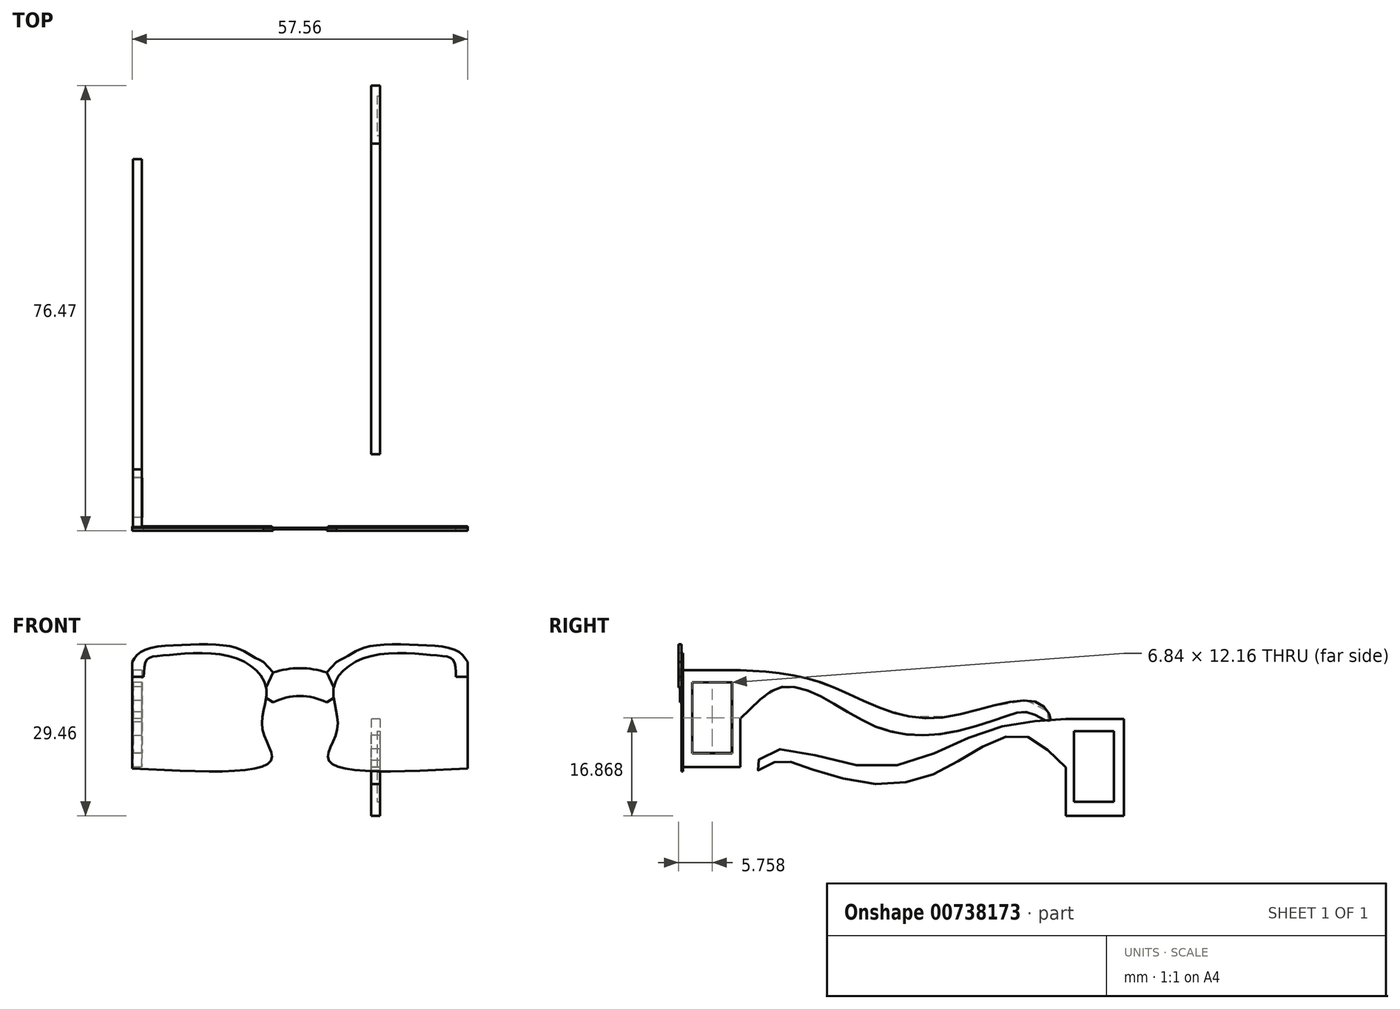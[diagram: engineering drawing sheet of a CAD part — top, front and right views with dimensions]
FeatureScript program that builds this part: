
annotation { "Feature Type Name" : "Feature", "Feature Type Description" : "" }
export const myFeature = defineFeature(function(context is Context, id is Id, definition is map)
    precondition{}
    {
        {
            var Q0;
            Q0=qCreatedBy(makeId("Front.planeOp"),FACE);
            var sketch = newSketch(context, id + "F0", { "sketchPlane" : qUnion([Q0])});
            skLineSegment(sketch, "E0", {"start": v(-26.3, 9.76) * mm, "end": v(-26.3, -8.53) * mm});
            skFitSpline(sketch, "E1", {"points": [v(-26.3, 9.76) * mm, v(-24.5, 11.69) * mm, v(-17.15, 12.72) * mm, v(-8.91, 12.33) * mm, v(-6.2, 11.04) * mm, v(-3.76, 9.76) * mm], "startDerivative": vector(8.68, 14.19) * mm, "endDerivative": vector(16.06, -8) * mm});
            skFitSpline(sketch, "E2", {"points": [v(-26.3, -8.53) * mm, v(-2.44, -7.08) * mm, v(-3.96, -1.66) * mm, v(-3.31, 5.38) * mm, v(-9.38, 10.68) * mm, v(-20.75, 10.9) * mm, v(-23.78, 10.14) * mm, v(-24.32, 7.22) * mm], "startDerivative": vector(136.2, -7.06) * mm, "endDerivative": vector(-0.76, -39.69) * mm});
            skLineSegment(sketch, "E3", {"start": v(-24.32, 7.22) * mm, "end": v(-26.3, 7.22) * mm});
            skPoint(sketch, "E3.endSnap0", {"position": v(-26.3, 0.61) * mm});
            skFitSpline(sketch, "E4", {"points": [v(-3.76, 9.76) * mm, v(-2.11, 7.94) * mm], "startDerivative": vector(1.65, -1.82) * mm, "endDerivative": vector(1.65, -1.82) * mm});
            skArc(sketch, "E5", {"start": v(7.08, 7.94) * mm, "mid": v(2.48, 8.7) * mm, "end": v(-2.11, 7.94) * mm});
            skFitSpline(sketch, "E6", {"points": [v(-2.11, 2.81) * mm, v(-3.32, 3.56) * mm], "startDerivative": vector(-1.22, 0.75) * mm, "endDerivative": vector(-1.22, 0.75) * mm});
            skFitSpline(sketch, "E7.MirrorCS", {"points": [v(31.26, -8.53) * mm, v(7.4, -7.08) * mm, v(8.93, -1.66) * mm, v(8.28, 5.38) * mm, v(14.34, 10.68) * mm, v(25.71, 10.9) * mm, v(28.74, 10.14) * mm, v(29.29, 7.22) * mm], "startDerivative": vector(-136.2, -7.06) * mm, "endDerivative": vector(0.76, -39.69) * mm});
            skLineSegment(sketch, "E8.MirrorCS", {"start": v(29.29, 7.22) * mm, "end": v(31.26, 7.22) * mm});
            skFitSpline(sketch, "E9.MirrorCS", {"points": [v(31.26, 9.76) * mm, v(29.46, 11.69) * mm, v(22.12, 12.72) * mm, v(13.88, 12.33) * mm, v(11.17, 11.04) * mm, v(8.72, 9.76) * mm], "startDerivative": vector(-8.68, 14.19) * mm, "endDerivative": vector(-16.06, -8) * mm});
            skFitSpline(sketch, "E10.MirrorCS", {"points": [v(8.72, 9.76) * mm, v(7.08, 7.94) * mm], "startDerivative": vector(-1.65, -1.82) * mm, "endDerivative": vector(-1.65, -1.82) * mm});
            skLineSegment(sketch, "E11.MirrorCS", {"start": v(31.26, 9.76) * mm, "end": v(31.26, -8.53) * mm});
            skFitSpline(sketch, "E12.MirrorCS", {"points": [v(7.08, 2.81) * mm, v(8.28, 3.56) * mm], "startDerivative": vector(1.22, 0.75) * mm, "endDerivative": vector(1.22, 0.75) * mm});
            skLineSegment(sketch, "E13", {"start": v(-2.11, 7.94) * mm, "end": v(-3.31, 5.38) * mm});
            skLineSegment(sketch, "E14", {"start": v(7.08, 7.94) * mm, "end": v(8.28, 5.38) * mm});
            skArc(sketch, "E15", {"start": v(7.08, 2.81) * mm, "mid": v(2.48, 3.92) * mm, "end": v(-2.11, 2.81) * mm});
            skSolve(sketch);
        }
        {
            var Q0;
            {var subQ3=sQuery(id+"F0.wireOp",EDGE,"E3");Q0=makeQuery(id+"F0.imprint","IMPRINT",FACE,{"disambiguationData":[TD([[makeQuery(id+"F0.imprint","IMPRINT",EDGE,{"derivedFrom":subQ3}),1.0]])]});}
            var Q1;
            {var subQ4=sQuery(id+"F0.wireOp",EDGE,"E8.MirrorCS");Q1=makeQuery(id+"F0.imprint","IMPRINT",FACE,{"disambiguationData":[TD([[makeQuery(id+"F0.imprint","IMPRINT",EDGE,{"derivedFrom":subQ4}),-1.0]])]});}
            extrude(context, id + "F1", {"entities" : qUnion([Q0, Q1]), "oppositeDirection" : true, "depth" : 0.25 * mm, "offsetDistance" : 25.4 * mm});
        }
        {
            var Q0;
            {var subQ1=sQuery(id+"F0.wireOp",EDGE,"E1");Q0=makeQuery(id+"F0.imprint","IMPRINT",FACE,{"disambiguationData":[TD([[makeQuery(id+"F0.imprint","IMPRINT",EDGE,{"derivedFrom":subQ1}),-1.0]])]});}
            var Q1;
            {var subQ1=sQuery(id+"F0.wireOp",EDGE,"E8.MirrorCS");Q1=makeQuery(id+"F0.imprint","IMPRINT",FACE,{"disambiguationData":[TD([[makeQuery(id+"F0.imprint","IMPRINT",EDGE,{"derivedFrom":subQ1}),1.0]])]});}
            extrude(context, id + "F2", {"entities" : qUnion([Q0, Q1]), "depth" : 0.5 * mm, "offsetDistance" : 25.4 * mm});
        }
        {
            var Q0;
            Q0=makeQuery(id+"F0.imprint","IMPRINT",FACE,{"disambiguationData":[TD([[makeQuery(id+"F0.imprint","IMPRINT",EDGE,{"derivedFrom":sQuery(id+"F0.wireOp",EDGE,"E5")}),1.0]])]});
            extrude(context, id + "F3", {"entities" : qUnion([Q0]), "depth" : 0.25 * mm, "offsetDistance" : 25.4 * mm});
        }
        {
            var Q0;
            Q0=qCreatedBy(makeId("Right.planeOp"),FACE);
            var sketch = newSketch(context, id + "F4", { "sketchPlane" : qUnion([Q0])});
            skLineSegment(sketch, "E16.bottom", {"start": v(-32.44, 0) * mm, "end": v(-29.65, 0) * mm});
            skLineSegment(sketch, "E16.top", {"start": v(-32.44, -16.69) * mm, "end": v(-29.65, -16.69) * mm});
            skLineSegment(sketch, "E16.left", {"start": v(-32.44, 0) * mm, "end": v(-32.44, -16.69) * mm});
            skLineSegment(sketch, "E16.right", {"start": v(-29.65, 0) * mm, "end": v(-29.65, -16.69) * mm});
            skLineSegment(sketch, "E17.bottom", {"start": v(-29.65, -16.69) * mm, "end": v(-22.46, -16.69) * mm});
            skLineSegment(sketch, "E17.top", {"start": v(-29.65, 0) * mm, "end": v(-22.46, 0) * mm});
            skLineSegment(sketch, "E17.left", {"start": v(-29.65, -16.69) * mm, "end": v(-29.65, 0) * mm});
            skLineSegment(sketch, "E17.right", {"start": v(-22.46, -16.69) * mm, "end": v(-22.46, 0) * mm});
            skFitSpline(sketch, "E18", {"points": [v(-22.46, 0) * mm, v(-8.27, -2.25) * mm, v(10.2, -8.29) * mm, v(28.68, -5.63) * mm, v(30.73, -8.79) * mm, v(27.4, -7.38) * mm, v(23.5, -7.84) * mm, v(11.29, -11.08) * mm, v(0, -9.36) * mm, v(-9.33, -4.18) * mm, v(-16.3, -3.22) * mm, v(-22.46, -8.34) * mm], "startDerivative": vector(117.48, -7.76) * mm, "endDerivative": vector(-70.3, -59.98) * mm});
            skLineSegment(sketch, "E19", {"start": v(-56.6, 20.3) * mm, "end": v(-56.6, -24.32) * mm});
            skLineSegment(sketch, "E20.MirrorCS", {"start": v(-80.76, 0) * mm, "end": v(-80.76, -16.69) * mm});
            skLineSegment(sketch, "E21.MirrorCS", {"start": v(-83.55, -16.69) * mm, "end": v(-83.55, 0) * mm});
            skLineSegment(sketch, "E22.MirrorCS", {"start": v(-80.76, -16.69) * mm, "end": v(-83.55, -16.69) * mm});
            skLineSegment(sketch, "E23.MirrorCS", {"start": v(-83.55, -16.69) * mm, "end": v(-90.74, -16.69) * mm});
            skLineSegment(sketch, "E24.MirrorCS", {"start": v(-80.76, 0) * mm, "end": v(-83.55, 0) * mm});
            skLineSegment(sketch, "E25.MirrorCS", {"start": v(-83.55, 0) * mm, "end": v(-90.74, 0) * mm});
            skLineSegment(sketch, "E26.MirrorCS", {"start": v(-90.74, -16.69) * mm, "end": v(-90.74, 0) * mm});
            skFitSpline(sketch, "E27.MirrorCS", {"points": [v(-90.74, 0) * mm, v(-104.93, -2.25) * mm, v(-123.4, -8.29) * mm, v(-141.88, -5.63) * mm, v(-143.93, -8.79) * mm, v(-140.6, -7.38) * mm, v(-136.7, -7.84) * mm, v(-124.49, -11.08) * mm, v(-113.2, -9.36) * mm, v(-103.87, -4.18) * mm, v(-96.9, -3.22) * mm, v(-90.74, -8.34) * mm], "startDerivative": vector(-117.48, -7.76) * mm, "endDerivative": vector(70.3, -59.98) * mm});
            skSolve(sketch);
        }
        {
            var Q0;
            {var subQ1=sQuery(id+"F4.wireOp",EDGE,"E17.bottom");Q0=makeQuery(id+"F4.imprint","IMPRINT",FACE,{"disambiguationData":[TD([[makeQuery(id+"F4.imprint","IMPRINT",EDGE,{"derivedFrom":subQ1}),1.0]])]});}
            var Q1;
            Q1=makeQuery(id+"F4.imprint","IMPRINT",FACE,{"disambiguationData":[TD([[makeQuery(id+"F4.imprint","IMPRINT",EDGE,{"derivedFrom":sQuery(id+"F4.wireOp",EDGE,"E16.bottom")}),-1.0]])]});
            var Q2;
            {var subQ0=sQuery(id+"F4.wireOp",EDGE,"E18");Q2=makeQuery(id+"F4.imprint","IMPRINT",FACE,{"disambiguationData":[TD([[makeQuery(id+"F4.imprint","IMPRINT",EDGE,{"derivedFrom":subQ0}),-1.0]])]});}
            var Q3;
            Q3=makeQuery(id+"F4.imprint","IMPRINT",FACE,{"disambiguationData":[TD([[makeQuery(id+"F4.imprint","IMPRINT",EDGE,{"derivedFrom":sQuery(id+"F4.wireOp",EDGE,"E20.MirrorCS")}),-1.0]])]});
            var Q4;
            Q4=makeQuery(id+"F4.imprint","IMPRINT",FACE,{"disambiguationData":[TD([[makeQuery(id+"F4.imprint","IMPRINT",EDGE,{"derivedFrom":sQuery(id+"F4.wireOp",EDGE,"E21.MirrorCS")}),1.0]])]});
            var Q5;
            {var subQ0=sQuery(id+"F4.wireOp",EDGE,"E27.MirrorCS");Q5=makeQuery(id+"F4.imprint","IMPRINT",FACE,{"disambiguationData":[TD([[makeQuery(id+"F4.imprint","IMPRINT",EDGE,{"derivedFrom":subQ0}),1.0]])]});}
            extrude(context, id + "F5", {"entities" : qUnion([Q0, Q1, Q2, Q3, Q4, Q5]), "depth" : 1.52 * mm, "offsetDistance" : 25.4 * mm});
        }
        {
            var Q0;
            Q0=makeQuery(id+"F5.opExtrude","SWEPT_BODY",BODY,{"disambiguationData":[OSD([sQuery(id+"F4.wireOp",EDGE,"E16.bottom"),sQuery(id+"F4.wireOp",EDGE,"E16.top"),sQuery(id+"F4.wireOp",EDGE,"E16.left"),sQuery(id+"F4.wireOp",EDGE,"E17.bottom"),sQuery(id+"F4.wireOp",EDGE,"E17.top"),sQuery(id+"F4.wireOp",EDGE,"E17.right"),sQuery(id+"F4.wireOp",EDGE,"E18")])]});
            transform(context, id + "F6", {"entities" : qUnion([Q0]), "transformType" : TransformType.TRANSLATION_3D, "dx" : -26.16 * mm, "dy" : 32.5 * mm, "dz" : 8.38 * mm, "makeCopy" : false});
        }
        {
            var Q0;
            Q0=makeQuery(id+"F5.opExtrude","CAP_FACE",FACE,{"disambiguationData":[OSD([sQuery(id+"F4.wireOp",EDGE,"E16.bottom"),sQuery(id+"F4.wireOp",EDGE,"E16.top"),sQuery(id+"F4.wireOp",EDGE,"E16.left"),sQuery(id+"F4.wireOp",EDGE,"E17.bottom"),sQuery(id+"F4.wireOp",EDGE,"E17.top"),sQuery(id+"F4.wireOp",EDGE,"E17.right"),sQuery(id+"F4.wireOp",EDGE,"E18")])],"isStart":true});
            var sketch = newSketch(context, id + "F7", { "sketchPlane" : qUnion([Q0])});
            skLineSegment(sketch, "E28.bottom", {"start": v(-8.67, 6.26) * mm, "end": v(-1.83, 6.26) * mm});
            skLineSegment(sketch, "E28.top", {"start": v(-8.67, -5.9) * mm, "end": v(-1.83, -5.9) * mm});
            skLineSegment(sketch, "E28.left", {"start": v(-8.67, 6.26) * mm, "end": v(-8.67, -5.9) * mm});
            skLineSegment(sketch, "E28.right", {"start": v(-1.83, 6.26) * mm, "end": v(-1.83, -5.9) * mm});
            skSolve(sketch);
        }
        {
            var Q0;
            Q0=makeQuery(id+"F7.imprint","IMPRINT",FACE,{"disambiguationData":[TD([[makeQuery(id+"F7.imprint","IMPRINT",EDGE,{"derivedFrom":sQuery(id+"F7.wireOp",EDGE,"E28.bottom")}),-1.0]])]});
            extrude(context, id + "F8", {"entities" : qUnion([Q0]), "operationType" : NewBodyOperationType.REMOVE, "oppositeDirection" : true, "depth" : 15.24 * mm, "offsetDistance" : 25.4 * mm});
        }
        {
            var Q0;
            Q0=qCreatedBy(makeId("Right.planeOp"),FACE);
            var sketch = newSketch(context, id + "F9", { "sketchPlane" : qUnion([Q0])});
            skLineSegment(sketch, "E29.bottom", {"start": v(-6.9, 1.93) * mm, "end": v(-13.73, 1.93) * mm});
            skLineSegment(sketch, "E29.top", {"start": v(-6.9, -10.23) * mm, "end": v(-13.73, -10.23) * mm});
            skLineSegment(sketch, "E29.left", {"start": v(-6.9, 1.93) * mm, "end": v(-6.9, -10.23) * mm});
            skLineSegment(sketch, "E29.right", {"start": v(-13.73, 1.93) * mm, "end": v(-13.73, -10.23) * mm});
            skSolve(sketch);
        }
        {
            var Q0;
            Q0=makeQuery(id+"F9.imprint","IMPRINT",FACE,{"disambiguationData":[TD([[makeQuery(id+"F9.imprint","IMPRINT",EDGE,{"derivedFrom":sQuery(id+"F9.wireOp",EDGE,"E29.bottom")}),1.0]])]});
            extrude(context, id + "F10", {"entities" : qUnion([Q0]), "depth" : 1.52 * mm, "offsetDistance" : 25.4 * mm});
        }
        {
            var Q0;
            Q0=makeQuery(id+"F10.opExtrude","SWEPT_BODY",BODY,{"disambiguationData":[OSD([sQuery(id+"F9.wireOp",EDGE,"E29.bottom"),sQuery(id+"F9.wireOp",EDGE,"E29.top"),sQuery(id+"F9.wireOp",EDGE,"E29.left"),sQuery(id+"F9.wireOp",EDGE,"E29.right")])]});
            transform(context, id + "F11", {"entities" : qUnion([Q0]), "transformType" : TransformType.TRANSLATION_3D, "dx" : -26.14 * mm, "dy" : 15.52 * mm, "dz" : 4.34 * mm, "makeCopy" : false});
        }
        {
            var Q0;
            Q0=makeQuery(id+"F5.opExtrude","SWEPT_BODY",BODY,{"disambiguationData":[OSD([sQuery(id+"F4.wireOp",EDGE,"E20.MirrorCS"),sQuery(id+"F4.wireOp",EDGE,"E22.MirrorCS"),sQuery(id+"F4.wireOp",EDGE,"E23.MirrorCS"),sQuery(id+"F4.wireOp",EDGE,"E24.MirrorCS"),sQuery(id+"F4.wireOp",EDGE,"E25.MirrorCS"),sQuery(id+"F4.wireOp",EDGE,"E26.MirrorCS"),sQuery(id+"F4.wireOp",EDGE,"E27.MirrorCS")])]});
            transform(context, id + "F12", {"entities" : qUnion([Q0]), "transformType" : TransformType.TRANSLATION_3D, "dx" : 14.73 * mm, "dy" : 156.72 * mm, "dz" : 0 * mm, "makeCopy" : false});
        }
        {
            var Q0;
            Q0=makeQuery(id+"F5.opExtrude","CAP_FACE",FACE,{"disambiguationData":[OSD([sQuery(id+"F4.wireOp",EDGE,"E20.MirrorCS"),sQuery(id+"F4.wireOp",EDGE,"E22.MirrorCS"),sQuery(id+"F4.wireOp",EDGE,"E23.MirrorCS"),sQuery(id+"F4.wireOp",EDGE,"E24.MirrorCS"),sQuery(id+"F4.wireOp",EDGE,"E25.MirrorCS"),sQuery(id+"F4.wireOp",EDGE,"E26.MirrorCS"),sQuery(id+"F4.wireOp",EDGE,"E27.MirrorCS")])],"isStart":false});
            var sketch = newSketch(context, id + "F13", { "sketchPlane" : qUnion([Q0])});
            skLineSegment(sketch, "E30.left", {"start": v(67.37, -2.1) * mm, "end": v(67.37, -14.28) * mm});
            skLineSegment(sketch, "E31", {"start": v(67.37, -14.28) * mm, "end": v(74.2, -14.28) * mm});
            skLineSegment(sketch, "E32", {"start": v(74.2, -14.28) * mm, "end": v(74.2, -2.1) * mm});
            skLineSegment(sketch, "E33", {"start": v(74.2, -2.1) * mm, "end": v(67.37, -2.1) * mm});
            skSolve(sketch);
        }
        {
            var Q0;
            Q0 = qSketchRegion(id + "F13", true);
            extrude(context, id + "F14", {"entities" : qUnion([Q0]), "oppositeDirection" : true, "depth" : 0.5 * mm, "offsetDistance" : 25.4 * mm});
        }
    });
